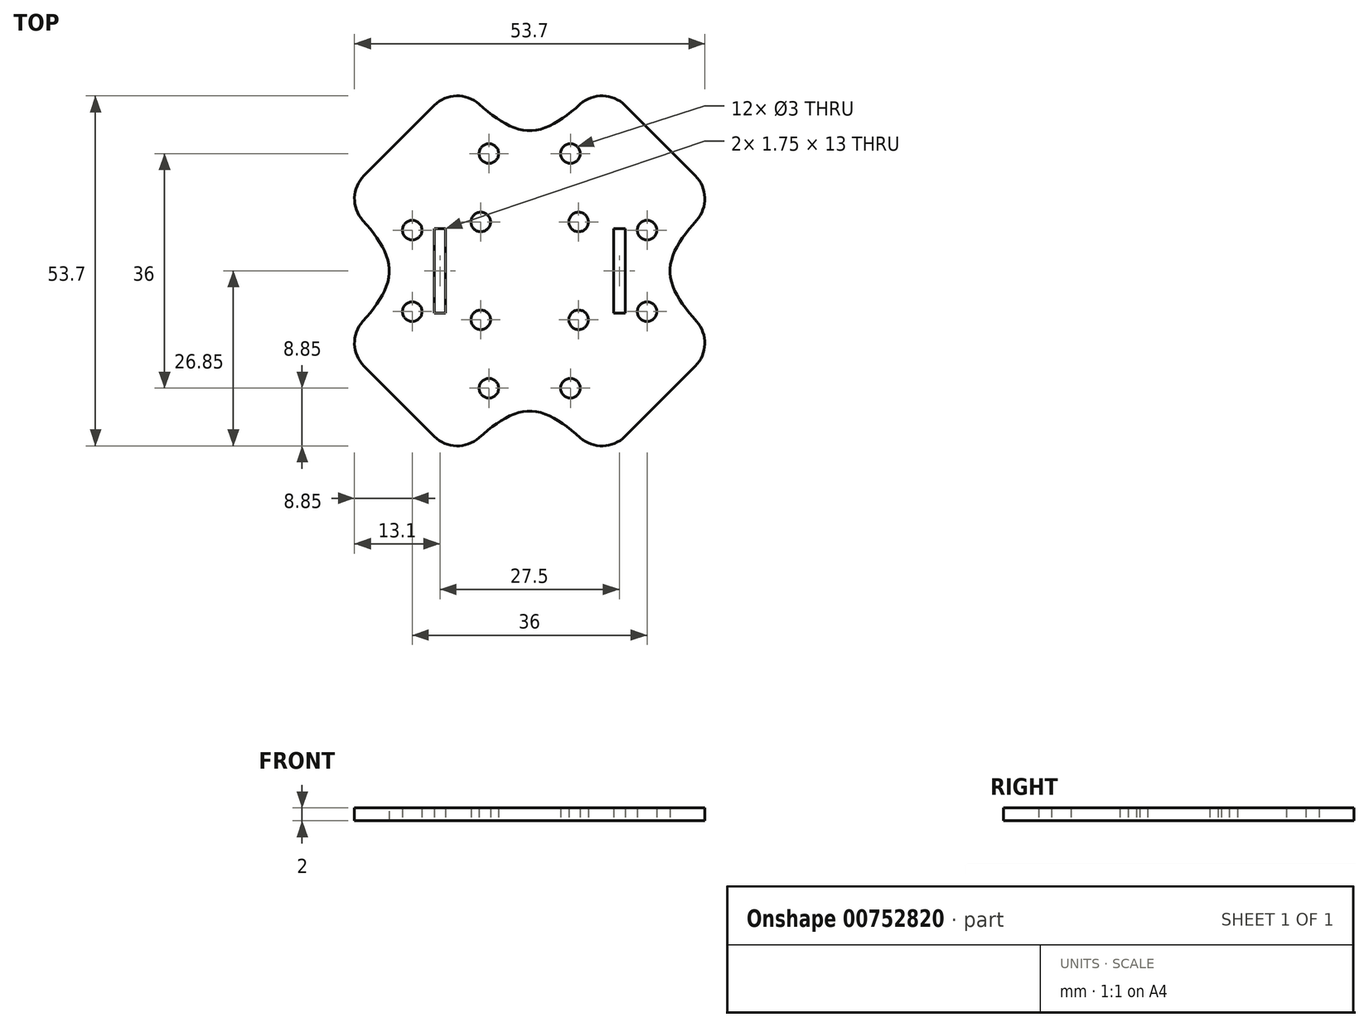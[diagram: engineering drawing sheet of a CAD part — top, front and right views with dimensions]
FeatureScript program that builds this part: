
annotation { "Feature Type Name" : "Feature", "Feature Type Description" : "" }
export const myFeature = defineFeature(function(context is Context, id is Id, definition is map)
    precondition{}
    {
        {
            var Q0;
            Q0=qCreatedBy(makeId("Top.planeOp"),FACE);
            var sketch = newSketch(context, id + "F0", { "sketchPlane" : qUnion([Q0])});
            skLineSegment(sketch, "E0.bottom", {"start": v(18, 18) * mm, "end": v(-18, 18) * mm, "construction": true});
            skLineSegment(sketch, "E0.top", {"start": v(18, -18) * mm, "end": v(-18, -18) * mm, "construction": true});
            skLineSegment(sketch, "E0.left", {"start": v(18, 18) * mm, "end": v(18, -18) * mm, "construction": true});
            skLineSegment(sketch, "E0.right", {"start": v(-18, 18) * mm, "end": v(-18, -18) * mm, "construction": true});
            skPoint(sketch, "E0.middle", {"position": v(0, 0) * mm});
            skLineSegment(sketch, "E1.bottom", {"start": v(15.25, 15.25) * mm, "end": v(-15.25, 15.25) * mm, "construction": true});
            skLineSegment(sketch, "E1.top", {"start": v(15.25, -15.25) * mm, "end": v(-15.25, -15.25) * mm, "construction": true});
            skLineSegment(sketch, "E1.left", {"start": v(15.25, 15.25) * mm, "end": v(15.25, -15.25) * mm, "construction": true});
            skLineSegment(sketch, "E1.right", {"start": v(-15.25, 15.25) * mm, "end": v(-15.25, -15.25) * mm, "construction": true});
            skCircle(sketch, "E2", {"center": v(-15.25, 15.25) * mm, "radius": 1.5 * mm, "construction": true});
            skCircle(sketch, "E3", {"center": v(15.25, 15.25) * mm, "radius": 1.5 * mm, "construction": true});
            skCircle(sketch, "E4", {"center": v(15.25, -15.25) * mm, "radius": 1.5 * mm, "construction": true});
            skCircle(sketch, "E5", {"center": v(-15.25, -15.25) * mm, "radius": 1.5 * mm, "construction": true});
            skLineSegment(sketch, "E6", {"start": v(0, 0) * mm, "end": v(-67.18, 67.18) * mm, "construction": true});
            skLineSegment(sketch, "E7", {"start": v(0, 0) * mm, "end": v(67.18, 67.18) * mm, "construction": true});
            skLineSegment(sketch, "E8", {"start": v(0, 0) * mm, "end": v(-67.18, -67.18) * mm, "construction": true});
            skLineSegment(sketch, "E9", {"start": v(0, 0) * mm, "end": v(67.18, -67.18) * mm, "construction": true});
            skCircle(sketch, "E10", {"center": v(-67.18, 67.18) * mm, "radius": 5 * mm});
            skCircle(sketch, "E11", {"center": v(-75.18, 67.18) * mm, "radius": 1.65 * mm});
            skCircle(sketch, "E12", {"center": v(-67.18, 76.68) * mm, "radius": 1.65 * mm});
            skCircle(sketch, "E13", {"center": v(-59.18, 67.18) * mm, "radius": 1.65 * mm});
            skCircle(sketch, "E14", {"center": v(-67.18, 57.68) * mm, "radius": 1.65 * mm});
            skCircle(sketch, "E15", {"center": v(67.18, 67.18) * mm, "radius": 5 * mm});
            skCircle(sketch, "E16", {"center": v(59.18, 67.18) * mm, "radius": 1.65 * mm});
            skCircle(sketch, "E17", {"center": v(67.18, 76.68) * mm, "radius": 1.65 * mm});
            skCircle(sketch, "E18", {"center": v(75.18, 67.18) * mm, "radius": 1.65 * mm});
            skCircle(sketch, "E19", {"center": v(67.18, 57.68) * mm, "radius": 1.65 * mm});
            skCircle(sketch, "E20", {"center": v(67.18, -67.18) * mm, "radius": 5 * mm});
            skCircle(sketch, "E21", {"center": v(59.18, -67.18) * mm, "radius": 1.65 * mm});
            skCircle(sketch, "E22", {"center": v(67.18, -57.68) * mm, "radius": 1.65 * mm});
            skCircle(sketch, "E23", {"center": v(75.18, -67.18) * mm, "radius": 1.65 * mm});
            skCircle(sketch, "E24", {"center": v(67.18, -76.68) * mm, "radius": 1.65 * mm});
            skCircle(sketch, "E25", {"center": v(-67.18, -67.18) * mm, "radius": 5 * mm});
            skCircle(sketch, "E26", {"center": v(-75.18, -67.18) * mm, "radius": 1.65 * mm});
            skCircle(sketch, "E27", {"center": v(-67.18, -57.68) * mm, "radius": 1.65 * mm});
            skCircle(sketch, "E28", {"center": v(-59.18, -67.18) * mm, "radius": 1.65 * mm});
            skCircle(sketch, "E29", {"center": v(-67.18, -76.68) * mm, "radius": 1.65 * mm});
            skCircle(sketch, "E30", {"center": v(-67.18, 67.18) * mm, "radius": 13.3 * mm, "construction": true});
            skCircle(sketch, "E31", {"center": v(-67.18, 67.18) * mm, "radius": 15.25 * mm});
            skCircle(sketch, "E32", {"center": v(67.18, 67.18) * mm, "radius": 13.3 * mm, "construction": true});
            skCircle(sketch, "E33", {"center": v(67.18, 67.18) * mm, "radius": 15.25 * mm});
            skCircle(sketch, "E34", {"center": v(-67.18, -67.18) * mm, "radius": 13.3 * mm, "construction": true});
            skCircle(sketch, "E35", {"center": v(-67.18, -67.18) * mm, "radius": 15.25 * mm});
            skCircle(sketch, "E36", {"center": v(67.18, -67.18) * mm, "radius": 13.3 * mm, "construction": true});
            skCircle(sketch, "E37", {"center": v(67.18, -67.18) * mm, "radius": 15.25 * mm});
            skLineSegment(sketch, "E38.bottom", {"start": v(20, 20) * mm, "end": v(-20, 20) * mm, "construction": true});
            skLineSegment(sketch, "E38.top", {"start": v(20, -20) * mm, "end": v(-20, -20) * mm, "construction": true});
            skLineSegment(sketch, "E38.left", {"start": v(20, 20) * mm, "end": v(20, -20) * mm, "construction": true});
            skLineSegment(sketch, "E38.right", {"start": v(-20, 20) * mm, "end": v(-20, -20) * mm, "construction": true});
            skLineSegment(sketch, "E39", {"start": v(-67.18, 67.18) * mm, "end": v(-77.96, 56.4) * mm, "construction": true});
            skLineSegment(sketch, "E40", {"start": v(-67.18, 67.18) * mm, "end": v(-56.4, 77.96) * mm, "construction": true});
            skPoint(sketch, "E41", {"position": v(0, 20) * mm});
            skPoint(sketch, "E42", {"position": v(-20, 0) * mm});
            skFitSpline(sketch, "E43", {"points": [v(-77.96, 56.4) * mm, v(-20, 0) * mm], "startDerivative": vector(73.8, -34.55) * mm, "endDerivative": vector(31.31, -75.4) * mm});
            skFitSpline(sketch, "E44", {"points": [v(-56.4, 77.96) * mm, v(0, 20) * mm], "startDerivative": vector(34.55, -73.8) * mm, "endDerivative": vector(75.4, -31.31) * mm});
            skLineSegment(sketch, "E45", {"start": v(67.18, 67.18) * mm, "end": v(56.4, 77.96) * mm, "construction": true});
            skLineSegment(sketch, "E46", {"start": v(67.18, 67.18) * mm, "end": v(77.96, 56.4) * mm, "construction": true});
            skFitSpline(sketch, "E47", {"points": [v(56.4, 77.96) * mm, v(0, 20) * mm], "startDerivative": vector(-34.5, -73.75) * mm, "endDerivative": vector(-75.31, -31.22) * mm});
            skFitSpline(sketch, "E48", {"points": [v(77.96, 56.4) * mm, v(20, 0) * mm], "startDerivative": vector(-73.75, -34.5) * mm, "endDerivative": vector(-31.22, -75.31) * mm});
            skCircle(sketch, "E49", {"center": v(-67.18, 67.18) * mm, "radius": 63.5 * mm, "construction": true});
            skCircle(sketch, "E50", {"center": v(67.18, 67.18) * mm, "radius": 63.5 * mm, "construction": true});
            skCircle(sketch, "E51", {"center": v(-67.18, -67.18) * mm, "radius": 63.5 * mm, "construction": true});
            skCircle(sketch, "E52", {"center": v(67.18, -67.18) * mm, "radius": 63.5 * mm, "construction": true});
            skLineSegment(sketch, "E53", {"start": v(67.18, -67.18) * mm, "end": v(56.4, -77.96) * mm, "construction": true});
            skLineSegment(sketch, "E54", {"start": v(67.18, -67.18) * mm, "end": v(77.96, -56.4) * mm, "construction": true});
            skLineSegment(sketch, "E55", {"start": v(-67.18, -67.18) * mm, "end": v(-77.96, -56.4) * mm, "construction": true});
            skLineSegment(sketch, "E56", {"start": v(-67.18, -67.18) * mm, "end": v(-56.4, -77.96) * mm, "construction": true});
            skFitSpline(sketch, "E57", {"points": [v(-77.96, -56.4) * mm, v(-20, 0) * mm], "startDerivative": vector(73.75, 34.5) * mm, "endDerivative": vector(31.22, 75.31) * mm});
            skFitSpline(sketch, "E58", {"points": [v(0, -20) * mm, v(-56.4, -77.96) * mm], "startDerivative": vector(-75.31, -31.22) * mm, "endDerivative": vector(-34.5, -73.75) * mm});
            skFitSpline(sketch, "E59", {"points": [v(0, -20) * mm, v(56.4, -77.96) * mm], "startDerivative": vector(75.31, -31.22) * mm, "endDerivative": vector(34.5, -73.75) * mm});
            skFitSpline(sketch, "E60", {"points": [v(20, 0) * mm, v(77.96, -56.4) * mm], "startDerivative": vector(31.22, -75.31) * mm, "endDerivative": vector(73.75, -34.5) * mm});
            skLineSegment(sketch, "E61", {"start": v(-20, 0) * mm, "end": v(20, 0) * mm});
            skLineSegment(sketch, "E62", {"start": v(0, 20) * mm, "end": v(0, -20) * mm});
            skLineSegment(sketch, "E63.bottom", {"start": v(-7.5, 7.5) * mm, "end": v(7.5, 7.5) * mm, "construction": true});
            skLineSegment(sketch, "E63.top", {"start": v(-7.5, -7.5) * mm, "end": v(7.5, -7.5) * mm, "construction": true});
            skLineSegment(sketch, "E63.left", {"start": v(-7.5, 7.5) * mm, "end": v(-7.5, -7.5) * mm, "construction": true});
            skLineSegment(sketch, "E63.right", {"start": v(7.5, 7.5) * mm, "end": v(7.5, -7.5) * mm, "construction": true});
            skCircle(sketch, "E64", {"center": v(-7.5, 7.5) * mm, "radius": 1.5 * mm});
            skCircle(sketch, "E65", {"center": v(7.5, 7.5) * mm, "radius": 1.5 * mm});
            skCircle(sketch, "E66", {"center": v(7.5, -7.5) * mm, "radius": 1.5 * mm});
            skCircle(sketch, "E67", {"center": v(-7.5, -7.5) * mm, "radius": 1.5 * mm});
            skLineSegment(sketch, "E68.bottom", {"start": v(6.25, 18) * mm, "end": v(-6.25, 18) * mm, "construction": true});
            skLineSegment(sketch, "E68.top", {"start": v(6.25, -18) * mm, "end": v(-6.25, -18) * mm, "construction": true});
            skLineSegment(sketch, "E68.left", {"start": v(6.25, 18) * mm, "end": v(6.25, -18) * mm, "construction": true});
            skLineSegment(sketch, "E68.right", {"start": v(-6.25, 18) * mm, "end": v(-6.25, -18) * mm, "construction": true});
            skCircle(sketch, "E69", {"center": v(-6.25, 18) * mm, "radius": 1.5 * mm});
            skCircle(sketch, "E70", {"center": v(6.25, 18) * mm, "radius": 1.5 * mm});
            skCircle(sketch, "E71", {"center": v(-6.25, -18) * mm, "radius": 1.5 * mm});
            skCircle(sketch, "E72", {"center": v(6.25, -18) * mm, "radius": 1.5 * mm});
            skLineSegment(sketch, "E73.bottom", {"start": v(-18, 6.25) * mm, "end": v(18, 6.25) * mm, "construction": true});
            skLineSegment(sketch, "E73.top", {"start": v(-18, -6.25) * mm, "end": v(18, -6.25) * mm, "construction": true});
            skLineSegment(sketch, "E73.left", {"start": v(-18, 6.25) * mm, "end": v(-18, -6.25) * mm, "construction": true});
            skLineSegment(sketch, "E73.right", {"start": v(18, 6.25) * mm, "end": v(18, -6.25) * mm, "construction": true});
            skCircle(sketch, "E74", {"center": v(-18, 6.25) * mm, "radius": 1.5 * mm});
            skCircle(sketch, "E75", {"center": v(-18, -6.25) * mm, "radius": 1.5 * mm});
            skCircle(sketch, "E76", {"center": v(18, 6.25) * mm, "radius": 1.5 * mm});
            skCircle(sketch, "E77", {"center": v(18, -6.25) * mm, "radius": 1.5 * mm});
            skLineSegment(sketch, "E78", {"start": v(-20, 20) * mm, "end": v(-11.16, 28.84) * mm});
            skLineSegment(sketch, "E79", {"start": v(-20, 20) * mm, "end": v(-28.84, 11.16) * mm});
            skLineSegment(sketch, "E80", {"start": v(20, 20) * mm, "end": v(11.16, 28.84) * mm});
            skLineSegment(sketch, "E81", {"start": v(20, 20) * mm, "end": v(28.84, 11.16) * mm});
            skLineSegment(sketch, "E82", {"start": v(20, -20) * mm, "end": v(28.84, -11.16) * mm});
            skLineSegment(sketch, "E83", {"start": v(20, -20) * mm, "end": v(11.16, -28.84) * mm});
            skLineSegment(sketch, "E84", {"start": v(-20, -20) * mm, "end": v(-28.84, -11.16) * mm});
            skLineSegment(sketch, "E85", {"start": v(-20, -20) * mm, "end": v(-11.16, -28.84) * mm});
            skLineSegment(sketch, "E86", {"start": v(0, -20) * mm, "end": v(0, -21.5) * mm, "construction": true});
            skLineSegment(sketch, "E87", {"start": v(-20, 0) * mm, "end": v(-21.5, 0) * mm, "construction": true});
            skLineSegment(sketch, "E88", {"start": v(0, 20) * mm, "end": v(0, 21.5) * mm, "construction": true});
            skLineSegment(sketch, "E89", {"start": v(20, 0) * mm, "end": v(21.5, 0) * mm, "construction": true});
            skFitSpline(sketch, "E90", {"points": [v(28.84, 11.16) * mm, v(21.5, 0) * mm, v(28.84, -11.16) * mm], "startDerivative": vector(-22.02, -22.32) * mm, "endDerivative": vector(22.02, -22.32) * mm});
            skFitSpline(sketch, "E91", {"points": [v(11.16, -28.84) * mm, v(0, -21.5) * mm, v(-11.16, -28.84) * mm], "startDerivative": vector(-22.32, 22.02) * mm, "endDerivative": vector(-22.32, -22.02) * mm});
            skFitSpline(sketch, "E92", {"points": [v(-28.84, -11.16) * mm, v(-21.5, 0) * mm, v(-28.84, 11.16) * mm], "startDerivative": vector(22.02, 22.32) * mm, "endDerivative": vector(-22.02, 22.32) * mm});
            skFitSpline(sketch, "E93", {"points": [v(-11.16, 28.84) * mm, v(0, 21.5) * mm, v(11.16, 28.84) * mm], "startDerivative": vector(22.32, -22.02) * mm, "endDerivative": vector(22.32, 22.02) * mm});
            skLineSegment(sketch, "E94", {"start": v(-15.25, 0) * mm, "end": v(-13.75, 0) * mm, "construction": true});
            skLineSegment(sketch, "E95.bottom", {"start": v(-14.62, -6.5) * mm, "end": v(-12.88, -6.5) * mm});
            skLineSegment(sketch, "E95.top", {"start": v(-14.62, 6.5) * mm, "end": v(-12.88, 6.5) * mm});
            skLineSegment(sketch, "E95.left", {"start": v(-14.62, -6.5) * mm, "end": v(-14.62, 6.5) * mm});
            skLineSegment(sketch, "E95.right", {"start": v(-12.88, -6.5) * mm, "end": v(-12.88, 6.5) * mm});
            skPoint(sketch, "E95.middle", {"position": v(-13.75, 0) * mm});
            skLineSegment(sketch, "E96", {"start": v(15.25, 0) * mm, "end": v(13.75, 0) * mm, "construction": true});
            skLineSegment(sketch, "E97.bottom", {"start": v(12.88, -6.5) * mm, "end": v(14.62, -6.5) * mm});
            skLineSegment(sketch, "E97.top", {"start": v(12.88, 6.5) * mm, "end": v(14.62, 6.5) * mm});
            skLineSegment(sketch, "E97.left", {"start": v(12.88, -6.5) * mm, "end": v(12.88, 6.5) * mm});
            skLineSegment(sketch, "E97.right", {"start": v(14.62, -6.5) * mm, "end": v(14.62, 6.5) * mm});
            skPoint(sketch, "E97.middle", {"position": v(13.75, 0) * mm});
            skSolve(sketch);
        }
        {
            var Q0;
            Q0=makeQuery(id+"F0.imprint","IMPRINT",FACE,{"disambiguationData":[TD([[makeQuery(id+"F0.imprint","IMPRINT",EDGE,{"derivedFrom":sQuery(id+"F0.wireOp",EDGE,"E64")}),-1.0]])]});
            var Q1;
            Q1=makeQuery(id+"F0.imprint","IMPRINT",FACE,{"disambiguationData":[TD([[makeQuery(id+"F0.imprint","IMPRINT",EDGE,{"derivedFrom":sQuery(id+"F0.wireOp",EDGE,"E67")}),-1.0]])]});
            var Q2;
            {var subQ0=sQuery(id+"F0.wireOp",EDGE,"E93");Q2=makeQuery(id+"F0.imprint","IMPRINT",FACE,{"disambiguationData":[TD([[makeQuery(id+"F0.imprint","IMPRINT",EDGE,{"derivedFrom":subQ0}),-1.0]])]});}
            var Q3;
            {var subQ0=sQuery(id+"F0.wireOp",EDGE,"E92");Q3=makeQuery(id+"F0.imprint","IMPRINT",FACE,{"disambiguationData":[TD([[makeQuery(id+"F0.imprint","IMPRINT",EDGE,{"derivedFrom":subQ0}),-1.0]])]});}
            var Q4;
            {var subQ0=sQuery(id+"F0.wireOp",EDGE,"E90");Q4=makeQuery(id+"F0.imprint","IMPRINT",FACE,{"disambiguationData":[TD([[makeQuery(id+"F0.imprint","IMPRINT",EDGE,{"derivedFrom":subQ0}),-1.0]])]});}
            var Q5;
            Q5=makeQuery(id+"F0.imprint","IMPRINT",FACE,{"disambiguationData":[TD([[makeQuery(id+"F0.imprint","IMPRINT",EDGE,{"derivedFrom":sQuery(id+"F0.wireOp",EDGE,"E66")}),-1.0]])]});
            var Q6;
            {var subQ0=sQuery(id+"F0.wireOp",EDGE,"E91");Q6=makeQuery(id+"F0.imprint","IMPRINT",FACE,{"disambiguationData":[TD([[makeQuery(id+"F0.imprint","IMPRINT",EDGE,{"derivedFrom":subQ0}),-1.0]])]});}
            var Q7;
            Q7=makeQuery(id+"F0.imprint","IMPRINT",FACE,{"disambiguationData":[TD([[makeQuery(id+"F0.imprint","IMPRINT",EDGE,{"derivedFrom":sQuery(id+"F0.wireOp",EDGE,"E65")}),-1.0]])]});
            extrude(context, id + "F1", {"entities" : qUnion([Q0, Q1, Q2, Q3, Q4, Q5, Q6, Q7]), "depth" : 2 * mm, "offsetDistance" : 25 * mm});
        }
        {
            var Q0;
            Q0=makeQuery(id+"F1.opExtrude","SWEPT_EDGE",EDGE,{"disambiguationData":[OSD([sQuery(id+"F0.wireOp",EDGE,"E78"),sQuery(id+"F0.wireOp",EDGE,"E93")])]});
            var Q1;
            Q1=makeQuery(id+"F1.opExtrude","SWEPT_EDGE",EDGE,{"disambiguationData":[OSD([sQuery(id+"F0.wireOp",EDGE,"E79"),sQuery(id+"F0.wireOp",EDGE,"E92")])]});
            var Q2;
            Q2=makeQuery(id+"F1.opExtrude","SWEPT_EDGE",EDGE,{"disambiguationData":[OSD([sQuery(id+"F0.wireOp",EDGE,"E80"),sQuery(id+"F0.wireOp",EDGE,"E93")])]});
            var Q3;
            Q3=makeQuery(id+"F1.opExtrude","SWEPT_EDGE",EDGE,{"disambiguationData":[OSD([sQuery(id+"F0.wireOp",EDGE,"E81"),sQuery(id+"F0.wireOp",EDGE,"E90")])]});
            var Q4;
            Q4=makeQuery(id+"F1.opExtrude","SWEPT_EDGE",EDGE,{"disambiguationData":[OSD([sQuery(id+"F0.wireOp",EDGE,"E82"),sQuery(id+"F0.wireOp",EDGE,"E90")])]});
            var Q5;
            Q5=makeQuery(id+"F1.opExtrude","SWEPT_EDGE",EDGE,{"disambiguationData":[OSD([sQuery(id+"F0.wireOp",EDGE,"E83"),sQuery(id+"F0.wireOp",EDGE,"E91")])]});
            var Q6;
            Q6=makeQuery(id+"F1.opExtrude","SWEPT_EDGE",EDGE,{"disambiguationData":[OSD([sQuery(id+"F0.wireOp",EDGE,"E85"),sQuery(id+"F0.wireOp",EDGE,"E91")])]});
            var Q7;
            Q7=makeQuery(id+"F1.opExtrude","SWEPT_EDGE",EDGE,{"disambiguationData":[OSD([sQuery(id+"F0.wireOp",EDGE,"E84"),sQuery(id+"F0.wireOp",EDGE,"E92")])]});
            fillet(context, id + "F2", {"entities" : qUnion([Q0, Q1, Q2, Q3, Q4, Q5, Q6, Q7]), "radius" : 5 * mm, "tangentPropagation" : true, "allowEdgeOverflow" : false});
        }
    });
